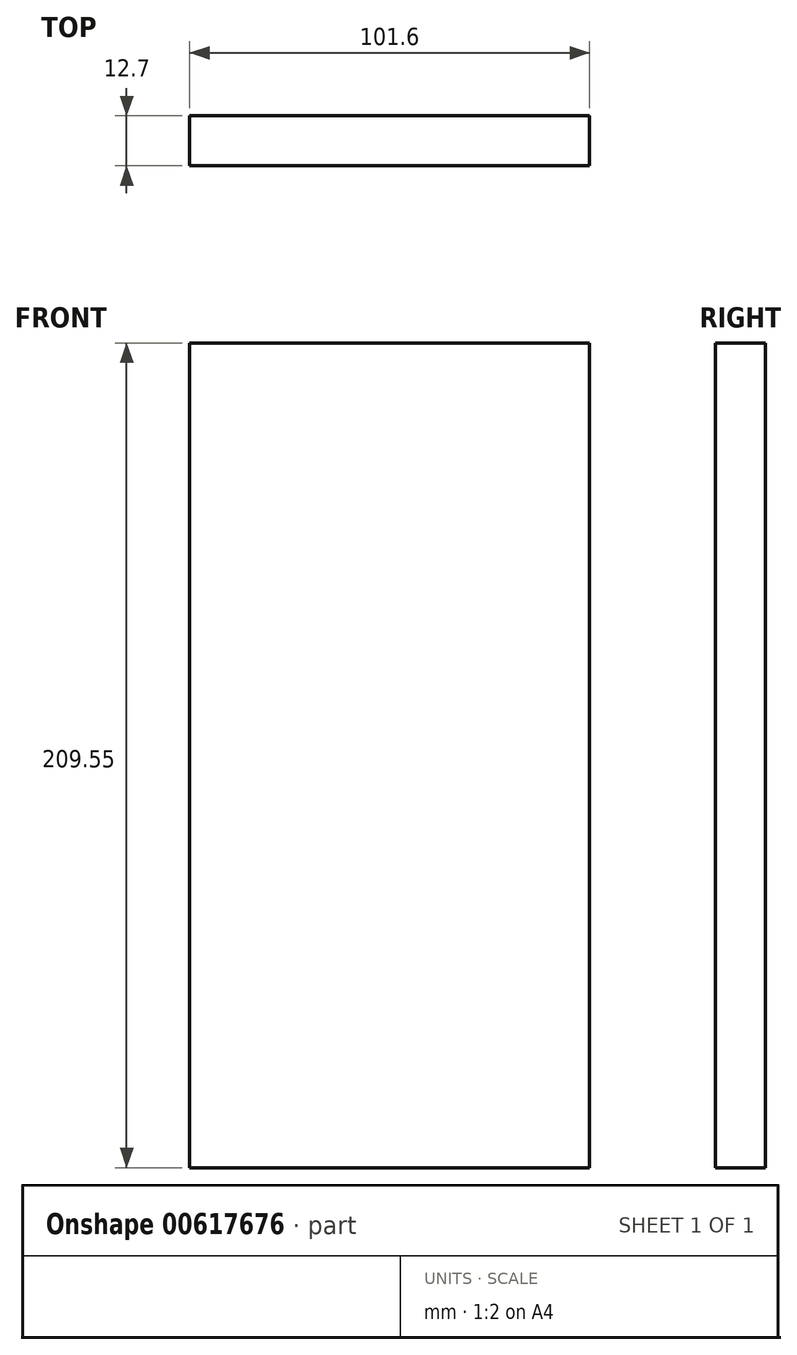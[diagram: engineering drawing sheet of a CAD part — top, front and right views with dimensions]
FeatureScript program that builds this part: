
annotation { "Feature Type Name" : "Feature", "Feature Type Description" : "" }
export const myFeature = defineFeature(function(context is Context, id is Id, definition is map)
    precondition{}
    {
        {
            var Q0;
            Q0=qCreatedBy(makeId("Front.planeOp"),FACE);
            var sketch = newSketch(context, id + "F0", { "sketchPlane" : qUnion([Q0])});
            skLineSegment(sketch, "E0.bottom", {"start": v(-26.11, 169.09) * mm, "end": v(75.49, 169.09) * mm});
            skLineSegment(sketch, "E0.top", {"start": v(-26.11, -40.46) * mm, "end": v(75.49, -40.46) * mm});
            skLineSegment(sketch, "E0.left", {"start": v(-26.11, 169.09) * mm, "end": v(-26.11, -40.46) * mm});
            skLineSegment(sketch, "E0.right", {"start": v(75.49, 169.09) * mm, "end": v(75.49, -40.46) * mm});
            skPoint(sketch, "E0.middle", {"position": v(24.69, 64.31) * mm});
            skSolve(sketch);
        }
        {
            var Q0;
            Q0 = qSketchRegion(id + "F0", true);
            extrude(context, id + "F1", {"entities" : qUnion([Q0]), "endBound" : BoundingType.SYMMETRIC, "depth" : 12.7 * mm, "offsetDistance" : 25.4 * mm});
        }
    });
